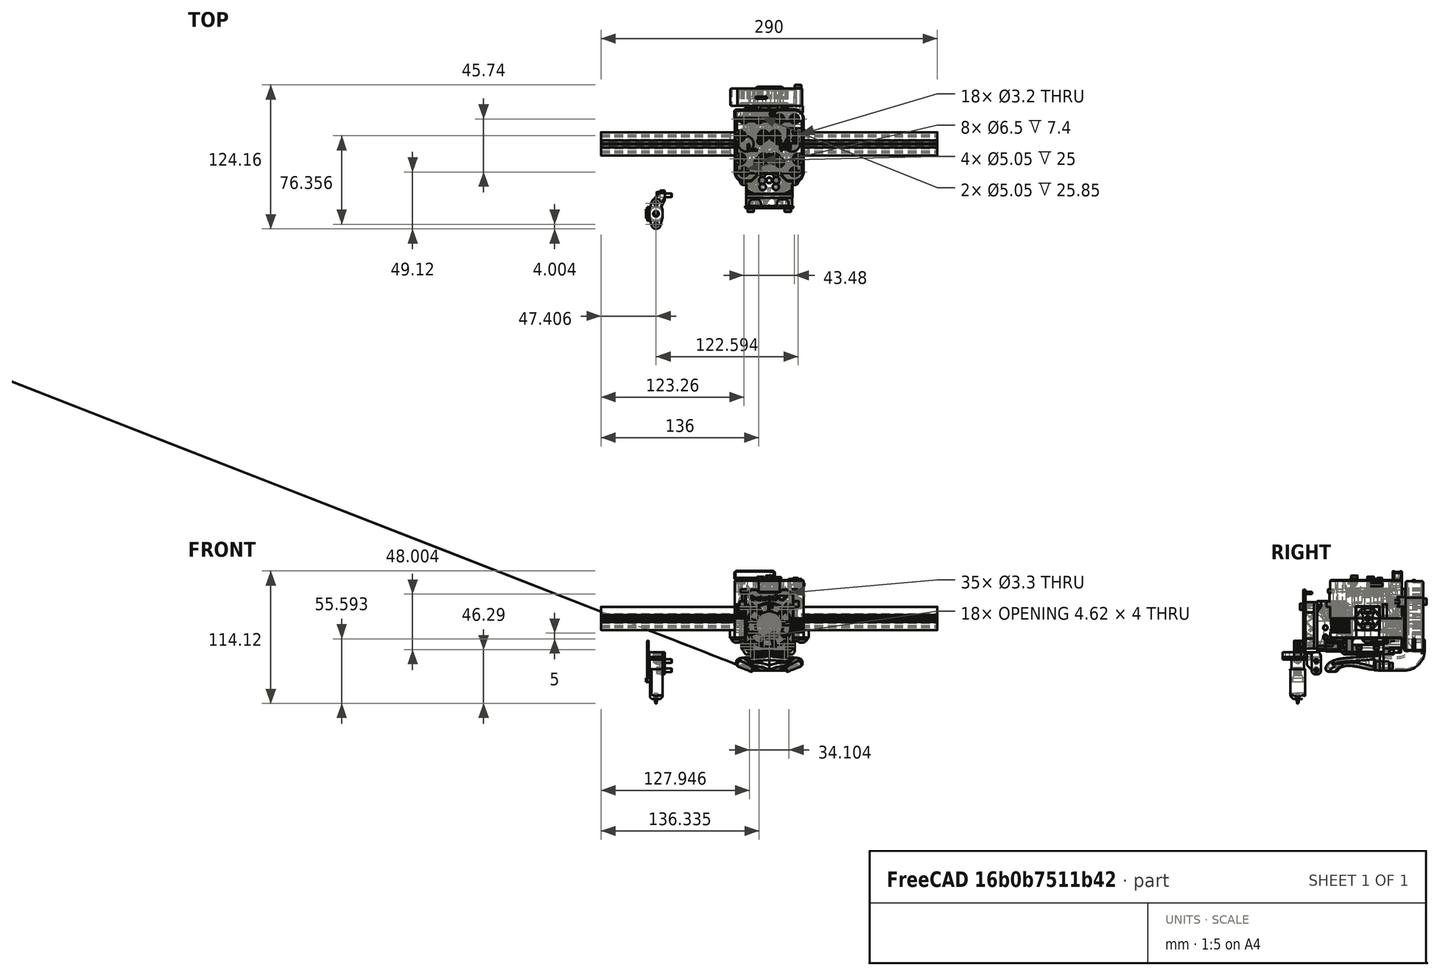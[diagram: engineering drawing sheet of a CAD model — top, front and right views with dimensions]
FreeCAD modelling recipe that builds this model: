
FCSTD DOCUMENT  (FreeCAD 0.19R24291 (Git))
Label: gantry-2020
License: Other
LicenseURL: GPL3
objects: Part::FeaturePython×86, Part::Feature×64, App::Part×6
note: 150 computed .brp shape members not serialized (recipe doc carries the construction recipe); baked Part::Feature solids carry a one-line shape summary decoded from their .brp

FEATURE [Part::Feature] Cut008004003004014002002005003004003002003001003001002001002002003050026007
  Placement = pos=(0,0,3) rot=(0,0,1;0rad)
  shape: bbox 58.24 x 61.74 x 33.85 mm, 150 faces (baked)
FEATURE [Part::Feature] Cut008004003004014002002005003004003002003001003001002001002002003050026008  label="smooth-idler012"
  Placement = pos=(-2,0.5,0) rot=(0,0,1;0rad)
  shape: bbox 15 x 15 x 10 mm, 8 faces (baked)
FEATURE [Part::FeaturePython] Washer404  label="M5-Washer071"  # Fasteners workbench fastener (typed FeaturePython)
  Placement = pos=(-20,0,40) rot=(0,0,1;0rad)
  baseObject = -> Cut008004003004014002002005003004003002003001003001002001002002003050026007 [Edge317]
  diameter = 1
  invert = false
  matchOuter = true
  offset = 0
  type = 4
FEATURE [Part::Feature] Chamfer030006001
  Placement = pos=(0,0,3) rot=(0,0,1;0rad)
  shape: bbox 31 x 61.74 x 17.85 mm, 87 faces (baked)
FEATURE [Part::FeaturePython] Screw1640  label="M5x50-Screw010"  # Fasteners workbench fastener (typed FeaturePython)
  Placement = pos=(21.74,-24.24,3) rot=(1,0,0;3.14159rad)
  baseObject = -> Chamfer030006001 [Edge99]
  diameter = 3
  invert = true
  length = 11
  lengthCustom = 50
  matchOuter = true
  offset = 0
  thread = false
  type = 39
FEATURE [Part::FeaturePython] Screw1641  label="M5x50-Screw001"  # Fasteners workbench fastener (typed FeaturePython)
  Placement = pos=(9,21.5,3) rot=(1,0,0;3.14159rad)
  baseObject = -> Chamfer030006001 [Edge100]
  diameter = 3
  invert = true
  length = 11
  lengthCustom = 50
  matchOuter = true
  offset = 0
  thread = false
  type = 39
FEATURE [Part::FeaturePython] Washer396  label="M5-Washer067"  # Fasteners workbench fastener (typed FeaturePython)
  Placement = pos=(15,0,3) rot=(1,0,0;3.14159rad)
  baseObject = -> Chamfer030006001 [Edge96]
  diameter = 1
  invert = false
  matchOuter = true
  offset = 0
  type = 4
FEATURE [Part::FeaturePython] Washer397  label="M5-Washer068"  # Fasteners workbench fastener (typed FeaturePython)
  Placement = pos=(28,0,3) rot=(1,0,0;3.14159rad)
  baseObject = -> Chamfer030006001 [Edge94]
  diameter = 1
  invert = false
  matchOuter = false
  offset = 0
  type = 4
FEATURE [Part::FeaturePython] Washer402  label="M3-Washer196"  # Fasteners workbench fastener (typed FeaturePython)
  Placement = pos=(5,-13,50) rot=(0,0,1;0rad)
  baseObject = -> Cut008004003004014002002005003004003002003001003001002001002002003050026007 [Edge369]
  diameter = 4
  invert = true
  matchOuter = true
  offset = 0
  type = 5
FEATURE [Part::Feature] Cut002001002
  Placement = pos=(0,0,3) rot=(0,0,1;0rad)
  shape: bbox 58.24 x 61.74 x 33.85 mm, 135 faces (baked)
FEATURE [Part::FeaturePython] Washer405  label="M3-Washer003"  # Fasteners workbench fastener (typed FeaturePython)
  Placement = pos=(-5,-13,50) rot=(0,0,1;0rad)
  baseObject = -> Cut002001002 [Edge296]
  diameter = 4
  invert = false
  matchOuter = true
  offset = 0
  type = 5
FEATURE [Part::FeaturePython] Screw1638  label="M3x10-Screw002"  # Fasteners workbench fastener (typed FeaturePython)
  Placement = pos=(-5,-13,50.55) rot=(0,0,1;0rad)
  baseObject = -> Washer405 [Edge1]
  diameter = 4
  invert = false
  length = 3
  lengthCustom = 10
  matchOuter = true
  offset = 0
  thread = false
  type = 33
FEATURE [Part::FeaturePython] Washer393  label="M3-Washer192"  # Fasteners workbench fastener (typed FeaturePython)
  Placement = pos=(-25,-13,50) rot=(0,0,1;0rad)
  baseObject = -> Cut002001002 [Edge298]
  diameter = 4
  invert = false
  matchOuter = true
  offset = 0
  type = 5
FEATURE [Part::FeaturePython] Screw1639  label="M3x10-Screw001"  # Fasteners workbench fastener (typed FeaturePython)
  Placement = pos=(-25,-13,50.55) rot=(0,0,1;0rad)
  baseObject = -> Washer393 [Edge1]
  diameter = 4
  invert = false
  length = 3
  lengthCustom = 10
  matchOuter = true
  offset = 0
  thread = false
  type = 33
FEATURE [Part::Feature] Cut008004003004014002002005003004003002003001003001002001002002003050026006  label="20t-idler012"
  Placement = pos=(0,-4.61,0) rot=(0,0,1;0rad)
  shape: bbox 15 x 15 x 10 mm, 31 faces (baked)
FEATURE [Part::FeaturePython] Screw1634  label="M5x50-Screw031"  # Fasteners workbench fastener (typed FeaturePython)
  Placement = pos=(9,-16,3) rot=(1,0,0;3.14159rad)
  baseObject = -> Chamfer030006001 [Edge97]
  diameter = 3
  invert = true
  length = 11
  lengthCustom = 50
  matchOuter = true
  offset = 0
  thread = false
  type = 39
FEATURE [Part::Feature] Chamfer008001
  Placement = pos=(0,0,3) rot=(0,0,1;0rad)
  shape: bbox 31 x 61.74 x 17.85 mm, 86 faces (baked)
FEATURE [Part::FeaturePython] Screw1644  label="M5x50-Screw032"  # Fasteners workbench fastener (typed FeaturePython)
  Placement = pos=(-9,21.5,3) rot=(1,0,0;3.14159rad)
  baseObject = -> Chamfer008001 [Edge84]
  diameter = 3
  invert = false
  length = 11
  lengthCustom = 50
  matchOuter = true
  offset = 0
  thread = false
  type = 39
FEATURE [Part::FeaturePython] Washer398  label="M5-Washer069"  # Fasteners workbench fastener (typed FeaturePython)
  Placement = pos=(-28,0,3) rot=(1,0,0;3.14159rad)
  baseObject = -> Chamfer008001 [Edge76]
  diameter = 1
  invert = false
  matchOuter = true
  offset = 0
  type = 4
FEATURE [Part::FeaturePython] Screw1650  label="M5x14-Screw001"  # Fasteners workbench fastener (typed FeaturePython)
  Placement = pos=(-28,0,1.9) rot=(1,0,0;3.14159rad)
  baseObject = -> Washer398 [Edge1]
  diameter = 3
  invert = false
  length = 3
  lengthCustom = 14
  matchOuter = true
  offset = 0
  thread = false
  type = 39
FEATURE [Part::FeaturePython] Screw1646  label="M5x50-Screw033"  # Fasteners workbench fastener (typed FeaturePython)
  Placement = pos=(-21.74,21.5,3) rot=(1,0,0;3.14159rad)
  baseObject = -> Chamfer008001 [Edge82]
  diameter = 3
  invert = false
  length = 11
  lengthCustom = 50
  matchOuter = true
  offset = 0
  thread = false
  type = 39
FEATURE [Part::FeaturePython] Screw1652  label="M5x50-Screw035"  # Fasteners workbench fastener (typed FeaturePython)
  Placement = pos=(-21.74,-24.24,3) rot=(1,0,0;3.14159rad)
  baseObject = -> Chamfer008001 [Edge83]
  diameter = 3
  invert = false
  length = 11
  lengthCustom = 50
  matchOuter = true
  offset = 0
  thread = false
  type = 39
FEATURE [Part::FeaturePython] Washer392  label="M5-Washer002"  # Fasteners workbench fastener (typed FeaturePython)
  Placement = pos=(20,0,40) rot=(0,0,1;0rad)
  baseObject = -> Cut002001002 [Edge208]
  diameter = 1
  invert = false
  matchOuter = true
  offset = 0
  type = 4
FEATURE [Part::FeaturePython] Screw1635  label="M5x16-Screw006"  # Fasteners workbench fastener (typed FeaturePython)
  Placement = pos=(20,0,41.1) rot=(0,0,1;0rad)
  baseObject = -> Washer392 [Edge1]
  diameter = 3
  invert = false
  length = 4
  lengthCustom = 16
  matchOuter = true
  offset = 0
  thread = false
  type = 39
FEATURE [Part::FeaturePython] Screw1633  label="M5x14-Screw"  # Fasteners workbench fastener (typed FeaturePython)
  Placement = pos=(28,0,1.9) rot=(1,0,0;3.14159rad)
  baseObject = -> Washer397 [Edge1]
  diameter = 3
  invert = false
  length = 3
  lengthCustom = 14
  matchOuter = true
  offset = 0
  thread = false
  type = 39
FEATURE [Part::FeaturePython] Washer394  label="M3-Washer001"  # Fasteners workbench fastener (typed FeaturePython)
  Placement = pos=(-25,7,50) rot=(0,0,1;0rad)
  baseObject = -> Cut002001002 [Edge302]
  diameter = 4
  invert = false
  matchOuter = true
  offset = 0
  type = 5
FEATURE [Part::FeaturePython] Screw1636  label="M3x10-Screw212"  # Fasteners workbench fastener (typed FeaturePython)
  Placement = pos=(-25,7,50.55) rot=(0,0,1;0rad)
  baseObject = -> Washer394 [Edge1]
  diameter = 4
  invert = false
  length = 3
  lengthCustom = 10
  matchOuter = true
  offset = 0
  thread = false
  type = 33
FEATURE [Part::FeaturePython] Washer399  label="M5-Washer070"  # Fasteners workbench fastener (typed FeaturePython)
  Placement = pos=(-15,0,3) rot=(1,0,0;3.14159rad)
  baseObject = -> Chamfer008001 [Edge80]
  diameter = 1
  invert = false
  matchOuter = true
  offset = 0
  type = 4
FEATURE [Part::FeaturePython] Screw1653  label="M5x12-Screw006"  # Fasteners workbench fastener (typed FeaturePython)
  Placement = pos=(-15,0,1.9) rot=(1,0,0;3.14159rad)
  baseObject = -> Washer399 [Edge1]
  diameter = 3
  invert = false
  length = 2
  lengthCustom = 12
  matchOuter = true
  offset = 0
  thread = false
  type = 39
FEATURE [Part::FeaturePython] Screw1642  label="M5x50-Screw002"  # Fasteners workbench fastener (typed FeaturePython)
  Placement = pos=(21.74,21.5,3) rot=(1,0,0;3.14159rad)
  baseObject = -> Chamfer030006001 [Edge98]
  diameter = 3
  invert = true
  length = 11
  lengthCustom = 50
  matchOuter = true
  offset = 0
  thread = false
  type = 39
FEATURE [Part::FeaturePython] Screw1654  label="M5x16-Screw"  # Fasteners workbench fastener (typed FeaturePython)
  Placement = pos=(-20,0,41.1) rot=(0,0,1;0rad)
  baseObject = -> Washer404 [Edge1]
  diameter = 3
  invert = false
  length = 4
  lengthCustom = 16
  matchOuter = true
  offset = 0
  thread = false
  type = 39
FEATURE [Part::FeaturePython] Screw1651  label="M5x50-Screw034"  # Fasteners workbench fastener (typed FeaturePython)
  Placement = pos=(-9,-16,3) rot=(1,0,0;3.14159rad)
  baseObject = -> Chamfer008001 [Edge81]
  diameter = 3
  invert = false
  length = 11
  lengthCustom = 50
  matchOuter = true
  offset = 0
  thread = false
  type = 39
FEATURE [Part::FeaturePython] Washer403  label="M3-Washer197"  # Fasteners workbench fastener (typed FeaturePython)
  Placement = pos=(25,-13,50) rot=(0,0,1;0rad)
  baseObject = -> Cut008004003004014002002005003004003002003001003001002001002002003050026007 [Edge371]
  diameter = 4
  invert = true
  matchOuter = true
  offset = 0
  type = 5
FEATURE [Part::FeaturePython] Washer395  label="M3-Washer193"  # Fasteners workbench fastener (typed FeaturePython)
  Placement = pos=(-5,7,50) rot=(0,0,1;0rad)
  baseObject = -> Cut002001002 [Edge300]
  diameter = 4
  invert = false
  matchOuter = true
  offset = 0
  type = 5
FEATURE [Part::FeaturePython] Screw1645  label="M3x10-Screw213"  # Fasteners workbench fastener (typed FeaturePython)
  Placement = pos=(25,-13,50.55) rot=(0,0,1;0rad)
  baseObject = -> Washer403 [Edge1]
  diameter = 4
  invert = false
  length = 3
  lengthCustom = 10
  matchOuter = true
  offset = 0
  thread = false
  type = 33
FEATURE [Part::FeaturePython] Washer400  label="M3-Washer194"  # Fasteners workbench fastener (typed FeaturePython)
  Placement = pos=(25,7,50) rot=(0,0,1;0rad)
  baseObject = -> Cut008004003004014002002005003004003002003001003001002001002002003050026007 [Edge375]
  diameter = 4
  invert = true
  matchOuter = true
  offset = 0
  type = 5
FEATURE [Part::FeaturePython] Screw1647  label="M3x10-Screw214"  # Fasteners workbench fastener (typed FeaturePython)
  Placement = pos=(25,7,50.55) rot=(0,0,1;0rad)
  baseObject = -> Washer400 [Edge1]
  diameter = 4
  invert = false
  length = 3
  lengthCustom = 10
  matchOuter = true
  offset = 0
  thread = false
  type = 33
FEATURE [Part::FeaturePython] Screw1643  label="M3x10-Screw216"  # Fasteners workbench fastener (typed FeaturePython)
  Placement = pos=(-5,7,50.55) rot=(0,0,1;0rad)
  baseObject = -> Washer395 [Edge1]
  diameter = 4
  invert = false
  length = 3
  lengthCustom = 10
  matchOuter = true
  offset = 0
  thread = false
  type = 33
FEATURE [Part::FeaturePython] Washer401  label="M3-Washer195"  # Fasteners workbench fastener (typed FeaturePython)
  Placement = pos=(5,7,50) rot=(0,0,1;0rad)
  baseObject = -> Cut008004003004014002002005003004003002003001003001002001002002003050026007 [Edge373]
  diameter = 4
  invert = true
  matchOuter = true
  offset = 0
  type = 5
FEATURE [Part::FeaturePython] Screw1648  label="M3x10-Screw215"  # Fasteners workbench fastener (typed FeaturePython)
  Placement = pos=(5,7,50.55) rot=(0,0,1;0rad)
  baseObject = -> Washer401 [Edge1]
  diameter = 4
  invert = false
  length = 3
  lengthCustom = 10
  matchOuter = true
  offset = 0
  thread = false
  type = 33
FEATURE [Part::FeaturePython] Screw1649  label="M3x10-Screw217"  # Fasteners workbench fastener (typed FeaturePython)
  Placement = pos=(5,-13,50.55) rot=(0,0,1;0rad)
  baseObject = -> Washer402 [Edge1]
  diameter = 4
  invert = false
  length = 3
  lengthCustom = 10
  matchOuter = true
  offset = 0
  thread = false
  type = 33
FEATURE [Part::Feature] Part__Mirroring003003003005043  label="smooth-idler013"
  Placement = pos=(2,0.5,0) rot=(0,0,1;0rad)
  shape: bbox 15 x 15 x 10 mm, 8 faces (baked)
FEATURE [Part::FeaturePython] Screw1637  label="M5x12-Screw"  # Fasteners workbench fastener (typed FeaturePython)
  Placement = pos=(15,0,1.9) rot=(1,0,0;3.14159rad)
  baseObject = -> Washer396 [Edge1]
  diameter = 3
  invert = false
  length = 2
  lengthCustom = 12
  matchOuter = true
  offset = 0
  thread = false
  type = 39
FEATURE [App::Part] Part243  label="Y-carrier-left"
  Group = -> [Cut008004003004014002002005003004003002003001003001002001002002003050026008,Cut008004003004014002002005003004003002003001003001002001002002003050026006,Chamfer030006001,Screw1633,Washer396,Screw1637,Washer397,Cut002001002,Washer393,Washer394,Washer395,Screw1635,Screw1636,Washer405,Screw1638,Screw1639,Screw1643,Washer392,Screw1640,Screw1641,Screw1642,Screw1634]
  Origin = -> Origin255
  Placement = pos=(-155,0,0) rot=(0,0,1;0rad)
FEATURE [Part::Feature] Part__Mirroring003003003005044  label="20t-idler013"
  Placement = pos=(0,-4.61,0) rot=(0,0,1;0rad)
  shape: bbox 15 x 15 x 10 mm, 31 faces (baked)
FEATURE [App::Part] Part244  label="Y-carrier-right"
  Group = -> [Part__Mirroring003003003005044,Part__Mirroring003003003005043,Chamfer008001,Cut008004003004014002002005003004003002003001003001002001002002003050026007,Washer399,Screw1650,Screw1653,Washer398,Screw1646,Screw1651,Screw1652,Screw1644,Screw1645,Screw1647,Screw1648,Screw1649,Washer401,Washer402,Washer403,Washer400,Washer404,Screw1654]
  Origin = -> Origin256
  Placement = pos=(155,0,0) rot=(0,0,1;0rad)
FEATURE [Part::Feature] Extrude002002002008  label="2020-290mm"
  Placement = pos=(-145,0,20) rot=(0,1,0;1.5708rad)
  shape: bbox 290 x 20 x 20 mm, 63 faces (baked)
FEATURE [Part::Feature] Fusion036012039011002025018010027013001002002001002001029002  label="switch004"
  Placement = pos=(28,7,46) rot=(0,0,1;1.5708rad)
  shape: bbox 12.18 x 13 x 6 mm, 43 faces (baked)
FEATURE [Part::Feature] Part__Feature112001144  label="adxl345 v035"
  shape: bbox 6 x 3 x 0.5 mm, 6 faces (baked)
FEATURE [Part::Feature] Part__Feature112001145  label="adxl345 v036"
  shape: bbox 0.5 x 0.5 x 0.15 mm, 6 faces (baked)
FEATURE [Part::Feature] Part__Feature112001146  label="adxl345 v037"
  shape: bbox 0.5 x 0.5 x 0.1 mm, 6 faces (baked)
FEATURE [Part::Feature] Part__Feature112001147  label="adxl345 v038"
  shape: bbox 0.5 x 0.5 x 0.1 mm, 6 faces (baked)
FEATURE [Part::Feature] Part__Feature112001148  label="adxl345 v039"
  shape: bbox 0.5 x 0.5 x 0.1 mm, 6 faces (baked)
FEATURE [Part::Feature] Part__Feature112001149  label="adxl345 v040"
  shape: bbox 0.5 x 0.5 x 0.1 mm, 6 faces (baked)
FEATURE [Part::Feature] Part__Feature112001150  label="adxl345 v041"
  shape: bbox 0.2125 x 0.3 x 0.1 mm, 6 faces (baked)
FEATURE [Part::Feature] Part__Feature112001151  label="adxl345 v042"
  shape: bbox 4 x 2 x 1 mm, 6 faces (baked)
FEATURE [Part::Feature] Part__Feature112001152  label="adxl345 v043"
  shape: bbox 0.2125 x 0.4 x 0.1 mm, 6 faces (baked)
FEATURE [Part::Feature] Part__Feature112001153  label="adxl345 v044"
  shape: bbox 0.5 x 0.5 x 0.15 mm, 6 faces (baked)
FEATURE [Part::Feature] Part__Feature112001154  label="adxl345 v045"
  shape: bbox 0.5 x 0.5054 x 0.15 mm, 6 faces (baked)
FEATURE [Part::Feature] Part__Feature112001155  label="adxl345 v046"
  shape: bbox 0.5 x 0.5 x 0.15 mm, 6 faces (baked)
FEATURE [Part::Feature] Part__Feature112001156  label="adxl345 v047"
  shape: bbox 0.5 x 0.5054 x 0.15 mm, 6 faces (baked)
FEATURE [Part::Feature] Part__Feature112001157  label="adxl345 v048"
  shape: bbox 0.5 x 0.5054 x 0.15 mm, 6 faces (baked)
FEATURE [Part::Feature] Part__Feature112001158  label="adxl345 v049"
  shape: bbox 0.5 x 0.5 x 0.1 mm, 6 faces (baked)
FEATURE [Part::Feature] Part__Feature112001159  label="4010 FAN002"
  Placement = pos=(-2.4e-14,-43.5,14) rot=(0,0,1;0rad)
  shape: bbox 40 x 10 x 40 mm, 104 faces (baked)
FEATURE [Part::FeaturePython] Screw1655  label="M3x20-Screw025"  # Fasteners workbench fastener (typed FeaturePython)
  Placement = pos=(-16,-55.5,30) rot=(1,0,0;1.5708rad)
  baseObject = -> Part__Feature112001159 [Edge130]
  diameter = 4
  invert = false
  length = 10
  lengthCustom = 20
  matchOuter = true
  offset = 2
  thread = false
  type = 33
FEATURE [Part::Feature] Part__Feature112001160  label="adxl345 v050"
  shape: bbox 0.5 x 2 x 0.1 mm, 6 faces (baked)
FEATURE [Part::Feature] Chamfer005021077002006007019003032007005
  Placement = pos=(0,29.5,32) rot=(1,0,0;1.5708rad)
  shape: bbox 38.38 x 11.83 x 29.43 mm, 84 faces (baked)
FEATURE [Part::Feature] Part__Feature112001161  label="adxl345 v051"
  shape: bbox 0.5 x 0.4946 x 0.1 mm, 6 faces (baked)
FEATURE [Part::Feature] Part__Feature112001162  label="adxl345 v052"
  shape: bbox 0.5005 x 0.5054 x 0.15 mm, 6 faces (baked)
FEATURE [Part::Feature] Fusion036012039011002025018010027013001002002001002001029003  label="mosquito-hotend002"
  Placement = pos=(0,-31.5,-28) rot=(0,0,1;0rad)
  shape: bbox 27.01 x 18.86 x 47.01 mm, 355 faces, 0 solids (baked)
FEATURE [Part::Feature] Part__Feature112001163  label="mosquito_support002"
  Placement = pos=(-2.78e-14,-21.6,27.5) rot=(0,0,1;0rad)
  shape: bbox 40 x 20.25 x 12 mm, 97 faces (baked)
FEATURE [Part::Feature] Part__Feature112001164  label="bottom_mgn12_short_duct002"
  Placement = pos=(0.00577366,-13.4565,-6.88873) rot=(0,0,1;0rad)
  shape: bbox 44.1 x 27 x 22.2 mm, 66 faces (baked)
FEATURE [Part::Feature] Part__Feature112001165  label="Duct v2.1 Straight002"
  Placement = pos=(15.0087,10.5436,-20.9887) rot=(0,0,1;0rad)
  shape: bbox 64.37 x 49.27 x 14.3 mm, 145 faces (baked)
FEATURE [Part::Feature] Part__Feature112001166  label="5015 fan002"
  Placement = pos=(-4.23967,32.8,25.9455) rot=(0.15487,0.698575,0.698575;3.44889rad)
  shape: bbox 61.97 x 15 x 62.93 mm, 220 faces (baked)
FEATURE [Part::FeaturePython] Screw1656  label="M4x12-Screw018"  # Fasteners workbench fastener (typed FeaturePython)
  Placement = pos=(1e-15,28.5,35) rot=(-1,0,0;1.5708rad)
  diameter = 5
  invert = false
  length = 11
  lengthCustom = 12
  matchOuter = true
  offset = 10
  thread = false
  type = 33
FEATURE [Part::FeaturePython] Screw1657  label="M4x12-Screw019"  # Fasteners workbench fastener (typed FeaturePython)
  Placement = pos=(-4,28.5,42) rot=(-1,0,0;1.5708rad)
  diameter = 5
  invert = false
  length = 11
  lengthCustom = 12
  matchOuter = true
  offset = 10
  thread = false
  type = 33
FEATURE [Part::FeaturePython] Screw1658  label="M4x12-Screw020"  # Fasteners workbench fastener (typed FeaturePython)
  Placement = pos=(4,28.5,42) rot=(-1,0,0;1.5708rad)
  diameter = 5
  invert = false
  length = 11
  lengthCustom = 12
  matchOuter = true
  offset = 10
  thread = false
  type = 33
FEATURE [Part::FeaturePython] Nut059  label="M3-Nut032"  # Fasteners workbench fastener (typed FeaturePython)
  Placement = pos=(24.8758,29.75,34.3023) rot=(1,0,0;1.5708rad)
  diameter = 4
  invert = false
  matchOuter = true
  offset = 0
  thread = false
  type = 7
FEATURE [Part::FeaturePython] Screw1659  label="M3x25-Screw031"  # Fasteners workbench fastener (typed FeaturePython)
  Placement = pos=(24.8765,47.8,34.436) rot=(-1,0,0;1.5708rad)
  baseObject = -> Part__Feature112001166 [Edge8]
  diameter = 4
  invert = false
  length = 10
  lengthCustom = 25
  matchOuter = true
  offset = 0
  thread = false
  type = 33
FEATURE [Part::FeaturePython] Screw017  label="M3x10-Screw218"  # Fasteners workbench fastener (typed FeaturePython)
  Placement = pos=(9.99577,10.0035,39.1513) rot=(0,0,1;0rad)
  diameter = 4
  invert = true
  length = 10
  lengthCustom = 10
  matchOuter = true
  offset = 0
  thread = false
  type = 33
FEATURE [Part::FeaturePython] Screw018  label="M3x10-Screw219"  # Fasteners workbench fastener (typed FeaturePython)
  Placement = pos=(9.99577,-9.99647,39.1513) rot=(0,0,1;0rad)
  diameter = 4
  invert = true
  length = 10
  lengthCustom = 10
  matchOuter = true
  offset = 0
  thread = false
  type = 33
FEATURE [Part::FeaturePython] Screw019  label="M3x10-Screw220"  # Fasteners workbench fastener (typed FeaturePython)
  Placement = pos=(-10.0042,10.0035,39.1513) rot=(0,0,1;0rad)
  diameter = 4
  invert = false
  length = 10
  lengthCustom = 10
  matchOuter = true
  offset = 0
  thread = false
  type = 33
FEATURE [Part::FeaturePython] Screw1660  label="M3x20-Screw026"  # Fasteners workbench fastener (typed FeaturePython)
  Placement = pos=(16,-55.5,30) rot=(1,0,0;1.5708rad)
  baseObject = -> Part__Feature112001159 [Edge124]
  diameter = 4
  invert = false
  length = 10
  lengthCustom = 20
  matchOuter = true
  offset = 2
  thread = false
  type = 33
FEATURE [Part::FeaturePython] Screw1661  label="M3x25-Screw032"  # Fasteners workbench fastener (typed FeaturePython)
  Placement = pos=(-16,-55.5,-2) rot=(1,0,0;1.5708rad)
  baseObject = -> Part__Feature112001159 [Edge127]
  diameter = 4
  invert = false
  length = 10
  lengthCustom = 25
  matchOuter = true
  offset = 2
  thread = false
  type = 33
FEATURE [Part::FeaturePython] Screw1662  label="M3x25-Screw033"  # Fasteners workbench fastener (typed FeaturePython)
  Placement = pos=(16,-55.5,-2) rot=(1,0,0;1.5708rad)
  baseObject = -> Part__Feature112001159 [Edge121]
  diameter = 4
  invert = false
  length = 10
  lengthCustom = 25
  matchOuter = true
  offset = 2
  thread = false
  type = 33
FEATURE [Part::FeaturePython] Screw1663  label="M2.5x12-Screw002"  # Fasteners workbench fastener (typed FeaturePython)
  Placement = pos=(-6,-31.5,29.2) rot=(0,0,1;0rad)
  diameter = 3
  invert = false
  length = 10
  lengthCustom = 12
  matchOuter = true
  offset = 10
  thread = false
  type = 33
FEATURE [Part::FeaturePython] Screw1664  label="M2.5x12-Screw003"  # Fasteners workbench fastener (typed FeaturePython)
  Placement = pos=(6,-31.5,29.2) rot=(0,0,1;0rad)
  diameter = 3
  invert = false
  length = 10
  lengthCustom = 12
  matchOuter = true
  offset = 10
  thread = false
  type = 33
FEATURE [Part::Feature] Part__Feature112001167  label="adxl345 v053"
  shape: bbox 0.1911 x 0.3 x 0.1 mm, 6 faces (baked)
FEATURE [Part::Feature] Part__Feature112001168  label="adxl345 v054"
  shape: bbox 0.5 x 0.5 x 0.1 mm, 6 faces (baked)
FEATURE [Part::Feature] Part__Feature112001169  label="adxl345 v055"
  shape: bbox 0.5 x 0.5 x 0.1 mm, 6 faces (baked)
FEATURE [Part::Feature] Part__Feature112001170  label="adxl345 v056"
  shape: bbox 0.5 x 0.5 x 0.1 mm, 6 faces (baked)
FEATURE [Part::Feature] Part__Feature112001171  label="adxl345 v057"
  shape: bbox 20 x 15 x 1.27 mm, 8 faces (baked)
FEATURE [Part::Feature] Part__Feature112001172  label="adxl345 v058"
  shape: bbox 0.1939 x 0.3 x 0.1 mm, 6 faces (baked)
FEATURE [Part::Feature] Part__Feature112001173  label="adxl345 v059"
  shape: bbox 0.5 x 0.5 x 0.1 mm, 6 faces (baked)
FEATURE [Part::Feature] Part__Feature112001174  label="adxl345 v060"
  shape: bbox 0.5 x 0.4946 x 0.1 mm, 6 faces (baked)
FEATURE [Part::Feature] Part__Feature112001175  label="adxl345 v061"
  shape: bbox 0.5 x 2 x 0.1 mm, 6 faces (baked)
FEATURE [Part::Feature] Part__Feature112001176  label="adxl345 v062"
  shape: bbox 0.5 x 0.4946 x 0.1 mm, 6 faces (baked)
FEATURE [Part::Feature] Part__Feature112001177  label="adxl345 v063"
  shape: bbox 0.5 x 0.5 x 0.1 mm, 6 faces (baked)
FEATURE [Part::Feature] Part__Feature112001178  label="adxl345 v064"
  shape: bbox 0.5005 x 0.4962 x 0.1 mm, 6 faces (baked)
FEATURE [Part::Feature] Part__Feature112001179  label="adxl345 v065"
  shape: bbox 0.1911 x 0.4 x 0.1 mm, 6 faces (baked)
FEATURE [Part::Feature] Part__Feature112001180  label="BL-touch v3.x003"
  Placement = pos=(-97.5942,-60.3565,-13.2887) rot=(0,0,1;1.5708rad)
  shape: bbox 16.53 x 26.01 x 53.81 mm, 111 faces (baked)
FEATURE [Part::FeaturePython] Nut060  label="M3-Nut033"  # Fasteners workbench fastener (typed FeaturePython)
  Placement = pos=(-17.05,15.5,41) rot=(-1,0,0;1.5708rad)
  diameter = 4
  invert = false
  matchOuter = true
  offset = 0
  thread = false
  type = 7
FEATURE [Part::FeaturePython] Screw1665  label="M3x12-Screw068"  # Fasteners workbench fastener (typed FeaturePython)
  Placement = pos=(-15,18.5,-21) rot=(-1,0,0;1.5708rad)
  diameter = 4
  invert = true
  length = 10
  lengthCustom = 12
  matchOuter = true
  offset = 0
  thread = false
  type = 33
FEATURE [Part::FeaturePython] Nut061  label="M3-Nut034"  # Fasteners workbench fastener (typed FeaturePython)
  Placement = pos=(13,15.5,-7) rot=(-1,0,0;1.5708rad)
  diameter = 4
  invert = false
  matchOuter = true
  offset = 0
  thread = false
  type = 7
FEATURE [Part::Feature] Fusion036012039011002025018010027013001002002001002001029004  label="adxl-mount-compact002"
  Placement = pos=(0,-31.5,33) rot=(0,0,1;0rad)
  shape: bbox 22 x 12.5 x 6.5 mm, 26 faces (baked)
FEATURE [Part::FeaturePython] Screw  label="M3x8-Screw133"  # Fasteners workbench fastener (typed FeaturePython)
  Placement = pos=(0,7.5,48.5) rot=(0,0,1;0rad)
  diameter = 1
  invert = false
  length = 1
  lengthCustom = 8
  matchOuter = true
  offset = 0
  thread = false
  type = 39
FEATURE [Part::FeaturePython] Screw1666  label="M3x6-Screw106"  # Fasteners workbench fastener (typed FeaturePython)
  Placement = pos=(-7.5,2.5,53) rot=(0,0,1;0rad)
  baseObject = -> Fusion036012039011002025018010027013001002002001002001029004 [Edge2]
  diameter = 4
  invert = false
  length = 1
  lengthCustom = 6
  matchOuter = true
  offset = 2.4
  thread = false
  type = 33
FEATURE [Part::FeaturePython] Screw1379  label="M3x6-Screw107"  # Fasteners workbench fastener (typed FeaturePython)
  Placement = pos=(7.5,2.5,52.6) rot=(0,0,1;0rad)
  baseObject = -> Fusion036012039011002025018010027013001002002001002001029004 [Edge47]
  diameter = 4
  invert = false
  length = 1
  lengthCustom = 6
  matchOuter = true
  offset = 2
  thread = false
  type = 33
FEATURE [Part::FeaturePython] Screw1667  label="M3x35-Screw006"  # Fasteners workbench fastener (typed FeaturePython)
  Placement = pos=(-17.0542,-16.5,41.0035) rot=(1,0,0;1.5708rad)
  diameter = 1
  invert = true
  length = 9
  lengthCustom = 35
  matchOuter = true
  offset = 0
  thread = false
  type = 39
FEATURE [Part::FeaturePython] Screw1668  label="M3x35-Screw007"  # Fasteners workbench fastener (typed FeaturePython)
  Placement = pos=(17.0458,-16.5,41.0035) rot=(1,0,0;1.5708rad)
  diameter = 1
  invert = true
  length = 9
  lengthCustom = 35
  matchOuter = true
  offset = 0
  thread = false
  type = 39
FEATURE [Part::Feature] Part__Feature112001181  label="dragon_support001"
  Placement = pos=(-1.3e-14,-65.5,-44.5) rot=(1,0,0;3.14159rad)
  shape: bbox 40 x 20.25 x 9.266 mm, 50 faces (baked)
FEATURE [Part::Feature] Chamfer005021077002006007019003032007006
  Placement = pos=(0,-56.5,-6) rot=(0,0,1;0rad)
  shape: bbox 41.5 x 7.5 x 53.5 mm, 789 faces (baked)
FEATURE [Part::Feature] Chamfer005021077002006007019003032007007  label="mosquito-face-compact-r004"
  Placement = pos=(0,-31.5,33) rot=(0,0,1;0rad)
  shape: bbox 51.01 x 27.77 x 40.81 mm, 154 faces (baked)
FEATURE [Part::Feature] Chamfer005021077002006007019003032007008  label="dragon-face-compacr-r004"
  Placement = pos=(0,-31.5,33) rot=(0,0,1;0rad)
  shape: bbox 51.01 x 26.2 x 43.01 mm, 143 faces (baked)
FEATURE [Part::Feature] Part__Feature112001182  label="bl_touch_mount002"
  Placement = pos=(-69.5942,-39.3565,-13.2887) rot=(0,0,1;0rad)
  shape: bbox 13.25 x 33 x 19 mm, 31 faces (baked)
FEATURE [Part::FeaturePython] Screw1669  label="M3x10-Screw221"  # Fasteners workbench fastener (typed FeaturePython)
  Placement = pos=(-94.0942,-44.3565,-24.7887) rot=(0,-1,0;1.5708rad)
  baseObject = -> Part__Feature112001182 [Edge2]
  diameter = 4
  invert = false
  length = 10
  lengthCustom = 10
  matchOuter = true
  offset = 0
  thread = false
  type = 33
FEATURE [Part::FeaturePython] Screw1670  label="M3x10-Screw222"  # Fasteners workbench fastener (typed FeaturePython)
  Placement = pos=(-94.0942,-44.3565,-16.7887) rot=(0,-1,0;1.5708rad)
  baseObject = -> Part__Feature112001182 [Edge1]
  diameter = 4
  invert = false
  length = 10
  lengthCustom = 10
  matchOuter = true
  offset = 0
  thread = false
  type = 33
FEATURE [App::Part] BL_Touch__1_002  label="BL-Touch <1>002"
  Group = -> [Part__Feature112001182,Part__Feature112001180,Screw1670,Screw1669]
  Origin = -> Origin258
  Placement = pos=(70,8,28.5) rot=(0,0,1;0rad)
FEATURE [Part::Feature] Chamfer008008001001  label="front-plate-2020-base002"
  Placement = pos=(0,-13,10) rot=(1,0,0;1.5708rad)
  shape: bbox 48 x 8 x 57 mm, 200 faces (baked)
FEATURE [Part::Feature] Chamfer005021077002006007019003032007009  label="belt-clamp-r004"
  Placement = pos=(19,-18.5,16) rot=(1,0,0;1.5708rad)
  shape: bbox 10.5 x 4.5 x 20 mm, 69 faces (baked)
FEATURE [Part::Feature] Chamfer005021077002006007019003032007010  label="belt-clamp-r005"
  Placement = pos=(-19,-18.5,4) rot=(0,0.707107,-0.707107;3.14159rad)
  shape: bbox 10.5 x 4.5 x 20 mm, 69 faces (baked)
FEATURE [Part::FeaturePython] Washer  label="M3-Washer"  # Fasteners workbench fastener (typed FeaturePython)
  Placement = pos=(19,-22.5,23) rot=(1,0,0;1.5708rad)
  baseObject = -> Chamfer005021077002006007019003032007009 [Edge84]
  diameter = 4
  invert = false
  matchOuter = true
  offset = 0
  type = 5
FEATURE [Part::FeaturePython] Washer406  label="M3-Washer198"  # Fasteners workbench fastener (typed FeaturePython)
  Placement = pos=(19,-22.5,9) rot=(1,0,0;1.5708rad)
  baseObject = -> Chamfer005021077002006007019003032007009 [Edge85]
  diameter = 4
  invert = false
  matchOuter = true
  offset = 0
  type = 5
FEATURE [Part::FeaturePython] Washer002  label="M3-Washer002"  # Fasteners workbench fastener (typed FeaturePython)
  Placement = pos=(-19,-22.5,11) rot=(1,0,0;1.5708rad)
  baseObject = -> Chamfer005021077002006007019003032007010 [Edge85]
  diameter = 4
  invert = false
  matchOuter = true
  offset = 0
  type = 5
FEATURE [Part::FeaturePython] Washer003  label="M3-Washer199"  # Fasteners workbench fastener (typed FeaturePython)
  Placement = pos=(-19,-22.5,-3) rot=(1,0,0;1.5708rad)
  baseObject = -> Chamfer005021077002006007019003032007010 [Edge84]
  diameter = 4
  invert = false
  matchOuter = true
  offset = 0
  type = 5
FEATURE [Part::Feature] Chamfer005021077002006007019003032007011  label="belt-tesioner-block003"
  Placement = pos=(6,15,7.5) rot=(0,1,0;3.14159rad)
  shape: bbox 20 x 14.4 x 10 mm, 116 faces (baked)
FEATURE [Part::Feature] Chamfer005021077002006007019003032007012  label="belt-tesioner-block004"
  Placement = pos=(-6,15,12.5) rot=(0,0,1;0rad)
  shape: bbox 20 x 14.4 x 10 mm, 116 faces (baked)
FEATURE [Part::Feature] Chamfer008011001002001002002003001001  label="backplate-2020-r2"
  Placement = pos=(1e-15,10,10) rot=(0,0.707107,0.707107;3.14159rad)
  shape: bbox 50.93 x 37.34 x 72.49 mm, 492 faces (baked)
FEATURE [Part::FeaturePython] Nut062  label="M3-Nut035"  # Fasteners workbench fastener (typed FeaturePython)
  Placement = pos=(-13,15.5,-7) rot=(-1,0,0;1.5708rad)
  diameter = 4
  invert = false
  matchOuter = true
  offset = 0
  thread = false
  type = 7
FEATURE [Part::FeaturePython] Screw1671  label="M3x35-Screw008"  # Fasteners workbench fastener (typed FeaturePython)
  Placement = pos=(-13.0042,-16,-6.99647) rot=(1,0,0;1.5708rad)
  diameter = 4
  invert = true
  length = 10
  lengthCustom = 35
  matchOuter = true
  offset = 0
  thread = false
  type = 33
FEATURE [Part::FeaturePython] Screw1672  label="M3x35-Screw009"  # Fasteners workbench fastener (typed FeaturePython)
  Placement = pos=(12.9958,-16,-6.99647) rot=(1,0,0;1.5708rad)
  diameter = 4
  invert = true
  length = 10
  lengthCustom = 35
  matchOuter = true
  offset = 0
  thread = false
  type = 33
FEATURE [Part::FeaturePython] Screw1673  label="M3x8-Screw124"  # Fasteners workbench fastener (typed FeaturePython)
  Placement = pos=(19,-22.5,23) rot=(1,0,0;1.5708rad)
  diameter = 4
  invert = false
  length = 10
  lengthCustom = 8
  matchOuter = true
  offset = 0
  thread = false
  type = 33
FEATURE [Part::FeaturePython] Screw1674  label="M3x8-Screw125"  # Fasteners workbench fastener (typed FeaturePython)
  Placement = pos=(19,-22.5,9) rot=(1,0,0;1.5708rad)
  diameter = 4
  invert = false
  length = 10
  lengthCustom = 8
  matchOuter = true
  offset = 0
  thread = false
  type = 33
FEATURE [Part::FeaturePython] Screw1675  label="M3x8-Screw126"  # Fasteners workbench fastener (typed FeaturePython)
  Placement = pos=(-19,-22.5,11) rot=(1,0,0;1.5708rad)
  diameter = 4
  invert = false
  length = 10
  lengthCustom = 8
  matchOuter = true
  offset = 0
  thread = false
  type = 33
FEATURE [Part::FeaturePython] Screw1676  label="M3x8-Screw127"  # Fasteners workbench fastener (typed FeaturePython)
  Placement = pos=(-19,-22.5,-3) rot=(1,0,0;1.5708rad)
  diameter = 4
  invert = false
  length = 10
  lengthCustom = 8
  matchOuter = true
  offset = 0
  thread = false
  type = 33
FEATURE [Part::FeaturePython] Screw020  label="M3x10-Screw"  # Fasteners workbench fastener (typed FeaturePython)
  Placement = pos=(-10.0042,-9.99647,39.1513) rot=(0,0,1;0rad)
  diameter = 4
  invert = false
  length = 10
  lengthCustom = 10
  matchOuter = true
  offset = 0
  thread = false
  type = 33
FEATURE [Part::FeaturePython] Screw021  label="M3x6-Screw104"  # Fasteners workbench fastener (typed FeaturePython)
  Placement = pos=(0,-11.5,54) rot=(0,0,1;0rad)
  diameter = 4
  invert = false
  length = 10
  lengthCustom = 6
  matchOuter = true
  offset = 0
  thread = false
  type = 33
FEATURE [Part::FeaturePython] Screw022  label="M3x12-Screw"  # Fasteners workbench fastener (typed FeaturePython)
  Placement = pos=(-21.9,-31.5,42) rot=(0,0,1;0rad)
  diameter = 4
  invert = false
  length = 10
  lengthCustom = 12
  matchOuter = true
  offset = 7
  thread = false
  type = 33
FEATURE [Part::FeaturePython] Screw023  label="M3x12-Screw069"  # Fasteners workbench fastener (typed FeaturePython)
  Placement = pos=(21.9,-31.5,42) rot=(0,0,1;0rad)
  diameter = 4
  invert = false
  length = 10
  lengthCustom = 12
  matchOuter = true
  offset = 7
  thread = false
  type = 33
FEATURE [Part::FeaturePython] Screw026  label="M3x8-Screw134"  # Fasteners workbench fastener (typed FeaturePython)
  Placement = pos=(3e-15,-20.15,-6) rot=(1,0,0;1.5708rad)
  baseObject = -> Part__Feature112001163 [Edge213]
  diameter = 4
  invert = true
  length = 10
  lengthCustom = 8
  matchOuter = true
  offset = 0
  thread = false
  type = 33
FEATURE [Part::FeaturePython] Screw1677  label="M3x25-Screw034"  # Fasteners workbench fastener (typed FeaturePython)
  Placement = pos=(-10.8,-38.5,27.5) rot=(1,0,0;1.5708rad)
  diameter = 4
  invert = false
  length = 10
  lengthCustom = 25
  matchOuter = true
  offset = 0
  thread = false
  type = 33
FEATURE [Part::FeaturePython] Screw1678  label="M3x25-Screw035"  # Fasteners workbench fastener (typed FeaturePython)
  Placement = pos=(10.8,-38.5,27.5) rot=(1,0,0;1.5708rad)
  diameter = 4
  invert = false
  length = 10
  lengthCustom = 25
  matchOuter = true
  offset = 0
  thread = false
  type = 33
FEATURE [Part::FeaturePython] Nut063  label="M3-Nut036"  # Fasteners workbench fastener (typed FeaturePython)
  Placement = pos=(17.05,15.5,41) rot=(-1,0,0;1.5708rad)
  diameter = 4
  invert = false
  matchOuter = true
  offset = 0
  thread = false
  type = 7
FEATURE [Part::FeaturePython] Screw1679  label="M3x40-Screw002"  # Fasteners workbench fastener (typed FeaturePython)
  Placement = pos=(-18.5,25.5,3.5) rot=(0,-1,0;1.5708rad)
  diameter = 4
  invert = false
  length = 10
  lengthCustom = 40
  matchOuter = true
  offset = 0
  thread = false
  type = 33
FEATURE [Part::FeaturePython] Screw1680  label="M3x40-Screw003"  # Fasteners workbench fastener (typed FeaturePython)
  Placement = pos=(18.5,25.5,16.5) rot=(0,1,0;1.5708rad)
  diameter = 4
  invert = false
  length = 10
  lengthCustom = 40
  matchOuter = true
  offset = 0
  thread = false
  type = 33
FEATURE [Part::FeaturePython] Nut064  label="M3-Nut037"  # Fasteners workbench fastener (typed FeaturePython)
  Placement = pos=(-14.8942,8.54353,-20.9887) rot=(1,0,0;1.5708rad)
  baseObject = -> Part__Feature112001165 [Edge4]
  diameter = 4
  invert = false
  matchOuter = true
  offset = 0
  thread = false
  type = 7
FEATURE [Part::FeaturePython] Nut065  label="M3-Nut038"  # Fasteners workbench fastener (typed FeaturePython)
  Placement = pos=(15.1058,8.54353,-20.9887) rot=(1,0,0;1.5708rad)
  baseObject = -> Part__Feature112001165 [Edge7]
  diameter = 4
  invert = false
  matchOuter = true
  offset = 0
  thread = false
  type = 7
FEATURE [Part::FeaturePython] Screw1681  label="M3x12-Screw070"  # Fasteners workbench fastener (typed FeaturePython)
  Placement = pos=(15,18.5,-21) rot=(-1,0,0;1.5708rad)
  diameter = 4
  invert = false
  length = 10
  lengthCustom = 12
  matchOuter = true
  offset = 0
  thread = false
  type = 33
FEATURE [Part::Feature] Part__Feature112001183  label="adxl345 v066"
  shape: bbox 2 x 1 x 0.3 mm, 6 faces (baked)
FEATURE [App::Part] adxl345_v004  label="adxl346"
  Group = -> [Part__Feature112001144,Part__Feature112001171,Part__Feature112001151,Part__Feature112001150,Part__Feature112001149,Part__Feature112001148,Part__Feature112001161,Part__Feature112001147,Part__Feature112001160,Part__Feature112001146,Part__Feature112001174,Part__Feature112001173,Part__Feature112001152,Part__Feature112001172,Part__Feature112001170,Part__Feature112001158,Part__Feature112001168,+15 more]
  Origin = -> Origin259
  Placement = pos=(-10,0.5,52.5) rot=(0,0,1;0rad)
FEATURE [Part::Feature] Body001002002  label="top-palte003"
  Placement = pos=(0,0,0) rot=(0,0,1;3.14159rad)
  shape: bbox 50.05 x 27 x 13 mm, 100 faces (baked)
FEATURE [Part::Feature] Body001002003  label="endstop-cap-compact003"
  Placement = pos=(16,7,54) rot=(1,0,0;3.14159rad)
  shape: bbox 12 x 13 x 7.75 mm, 19 faces (baked)
FEATURE [Part::FeaturePython] Screw1682  label="M2x10-Screw002"  # Fasteners workbench fastener (typed FeaturePython)
  Placement = pos=(22.75,3.75,53) rot=(0,0,1;0rad)
  baseObject = -> Body001002003 [Edge27]
  diameter = 2
  invert = false
  length = 5
  lengthCustom = 10
  matchOuter = true
  offset = 0
  thread = false
  type = 33
FEATURE [Part::FeaturePython] Screw1683  label="M2x10-Screw003"  # Fasteners workbench fastener (typed FeaturePython)
  Placement = pos=(22.75,10.25,53) rot=(0,0,1;0rad)
  baseObject = -> Body001002003 [Edge25]
  diameter = 2
  invert = false
  length = 5
  lengthCustom = 10
  matchOuter = true
  offset = 0
  thread = false
  type = 33
FEATURE [App::Part] Part245  label="toolhead-2020"
  Group = -> [Fusion036012039011002025018010027013001002002001002001029003,Part__Feature112001163,Part__Feature112001164,Part__Feature112001165,Part__Feature112001166,Part__Feature112001159,BL_Touch__1_002,Nut059,Nut063,Screw1681,Screw1665,Nut062,Nut061,Screw1679,Screw1680,Screw1656,Screw1658,Screw1657,Nut060,Screw1672,Screw1671,Nut065,Nut064,Screw1674,Screw1673,Screw1676,Screw1675,Screw1659,Screw022,Screw018,+41 more]
  Origin = -> Origin257
  Placement = pos=(55,0,10) rot=(0,0,1;0rad)
FEATURE [App::Part] Part002  label="gantry-2020"
  Group = -> [Part244,Part243,Extrude002002002008,Part245]
  Origin = -> Origin002
